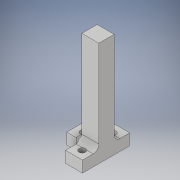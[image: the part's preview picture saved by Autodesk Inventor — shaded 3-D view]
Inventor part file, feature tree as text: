
AUTODESK INVENTOR PART (.ipt)
format: ipt  version: 2018 (Build 220112000, 112)  size: 229,376 bytes
history: native  units: mm
features: extrude x5, sketch x5, other x4, projected_geometry x3, reference x2, fillet x1
ambient origin geometry x8: Origin, YZ Plane, XZ Plane, XY Plane, X Axis, Y Axis, Z Axis, Center Point
bodies: Volumenkörper1 (feature_tree)
feature tree (20):
  extrude  "Extrusion1"  Depth=25.0mm
  extrude  "Extrusion2"  Depth=4.5mm
  extrude  "Extrusion3"  Depth=8.0mm
  fillet  "Rundung2"  Radius=75.0mm
  extrude  "Extrusion4"  Depth=75.0mm TaperAngle=0.0deg
  extrude  "Extrusion5"  Depth=10.0mm
  sketch  "Skizze1"  dims[d0=9.0mm d1=25.0mm]
  reference  "Referenz1"
  sketch  "Skizze2"  dims[d2=4.5mm d3=4.5mm]
  projected_geometry  "Projizierte Kontur1"
  projected_geometry  "Projizierte Kontur2"
  sketch  "Skizze3"  dims[d4=25.0mm d5=8.0mm d6=75.0mm d7=0.0mm]
  projected_geometry  "Projizierte Kontur3"
  reference  "Referenz2"
  sketch  "Skizze4"  dims[d8=6.0mm d9=75.0mm d10=0.0mm]
  sketch  "Skizze5"  dims[d12=75.0mm d13=0.0mm d14=5.2mm d16=3.0mm d17=10.0mm d18=0.0mm d19=10.0mm d20=0.0mm d21=3.4mm]
  other  "<userpath>\OneDrive\Development\Mohne\03_Konstruktion\Mohne komplett.iam"
  other  "Mohne komplett.iam"
  other  "chassis mit motorlöcher:1"
  other  "Wheel ALL1_MIR:1"
